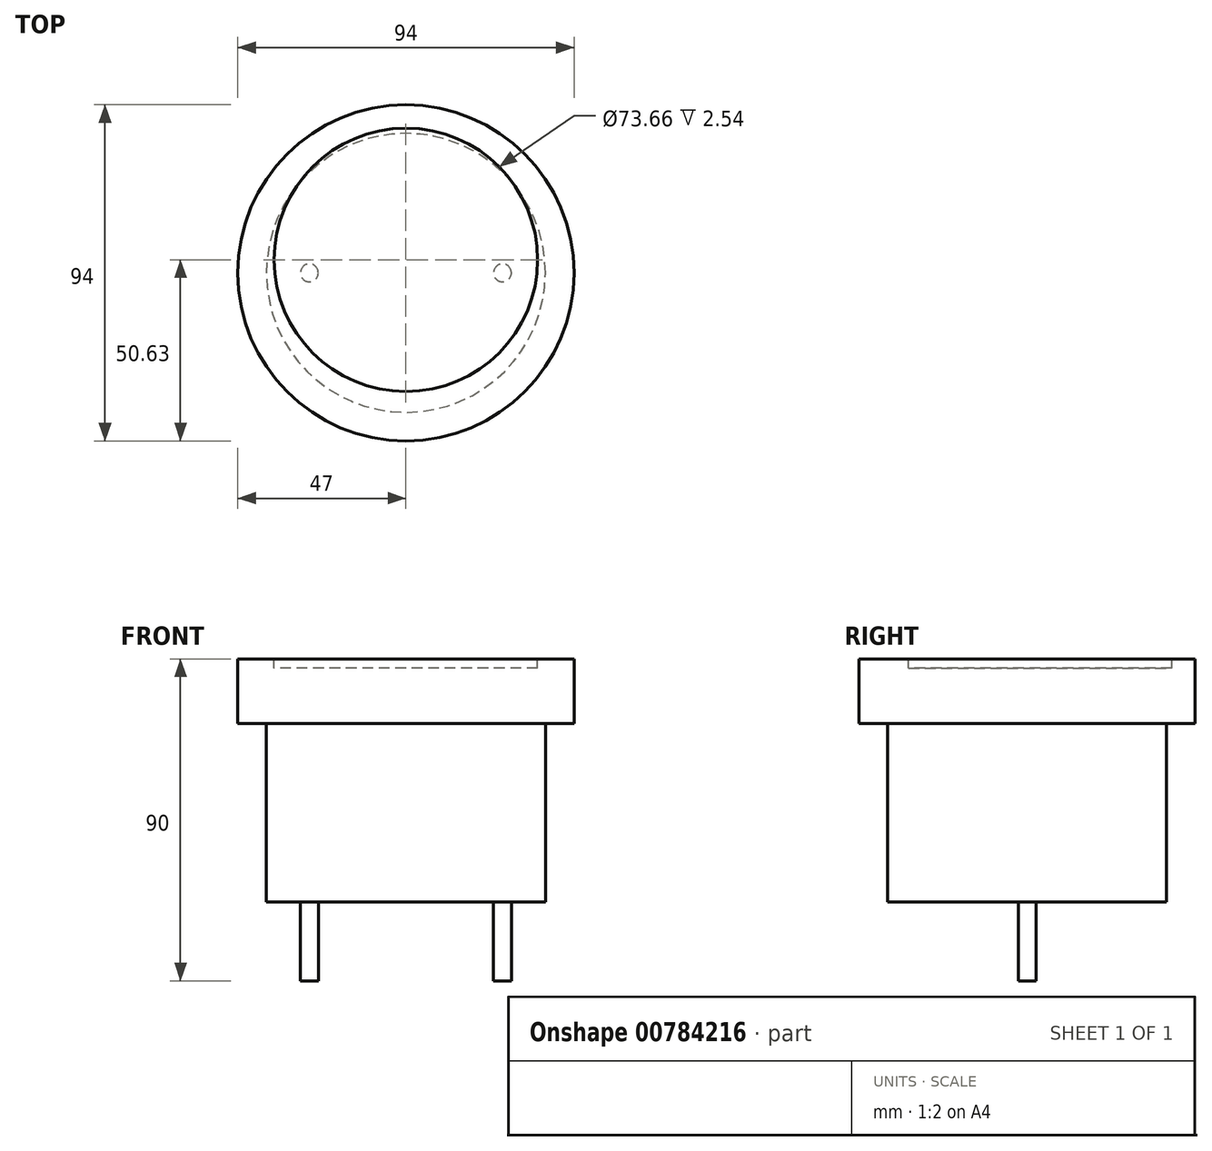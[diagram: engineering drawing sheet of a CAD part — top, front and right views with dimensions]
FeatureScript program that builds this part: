
annotation { "Feature Type Name" : "Feature", "Feature Type Description" : "" }
export const myFeature = defineFeature(function(context is Context, id is Id, definition is map)
    precondition{}
    {
        {
            var Q0;
            Q0=qCreatedBy(makeId("Top.planeOp"),FACE);
            var sketch = newSketch(context, id + "F0", { "sketchPlane" : qUnion([Q0])});
            skCircle(sketch, "E0", {"center": v(0, 0) * mm, "radius": 47 * mm});
            skSolve(sketch);
        }
        {
            var Q0;
            Q0=makeQuery(id+"F0.imprint","IMPRINT",FACE,{"disambiguationData":[TD([[makeQuery(id+"F0.imprint","IMPRINT",EDGE,{"derivedFrom":sQuery(id+"F0.wireOp",EDGE,"E0")}),1.0]])]});
            extrude(context, id + "F1", {"entities" : qUnion([Q0]), "depth" : 18 * mm, "offsetDistance" : 25.4 * mm});
        }
        {
            var Q0;
            Q0=makeQuery(id+"F1.opExtrude","CAP_FACE",FACE,{"disambiguationData":[OSD([sQuery(id+"F0.wireOp",EDGE,"E0")])],"isStart":true});
            var sketch = newSketch(context, id + "F2", { "sketchPlane" : qUnion([Q0])});
            skCircle(sketch, "E1", {"center": v(0, 0) * mm, "radius": 39 * mm});
            skSolve(sketch);
        }
        {
            var Q0;
            Q0=makeQuery(id+"F2.imprint","IMPRINT",FACE,{"disambiguationData":[TD([[makeQuery(id+"F2.imprint","IMPRINT",EDGE,{"derivedFrom":sQuery(id+"F2.wireOp",EDGE,"E1")}),1.0]])]});
            extrude(context, id + "F3", {"entities" : qUnion([Q0]), "operationType" : NewBodyOperationType.ADD, "depth" : 50 * mm, "offsetDistance" : 25.4 * mm});
        }
        {
            var Q0;
            Q0=makeQuery(id+"F3.opExtrude","CAP_FACE",FACE,{"disambiguationData":[OSD([sQuery(id+"F2.wireOp",EDGE,"E1")])],"isStart":false});
            var sketch = newSketch(context, id + "F4", { "sketchPlane" : qUnion([Q0])});
            skCircle(sketch, "E2", {"center": v(-27, 0) * mm, "radius": 2.5 * mm});
            skCircle(sketch, "E3", {"center": v(27, 0) * mm, "radius": 2.5 * mm});
            skSolve(sketch);
        }
        {
            var Q0;
            Q0=makeQuery(id+"F4.imprint","IMPRINT",FACE,{"disambiguationData":[TD([[makeQuery(id+"F4.imprint","IMPRINT",EDGE,{"derivedFrom":sQuery(id+"F4.wireOp",EDGE,"E2")}),1.0]])]});
            var Q1;
            Q1=makeQuery(id+"F4.imprint","IMPRINT",FACE,{"disambiguationData":[TD([[makeQuery(id+"F4.imprint","IMPRINT",EDGE,{"derivedFrom":sQuery(id+"F4.wireOp",EDGE,"E3")}),1.0]])]});
            extrude(context, id + "F5", {"entities" : qUnion([Q0, Q1]), "operationType" : NewBodyOperationType.ADD, "depth" : 22 * mm, "offsetDistance" : 25.4 * mm});
        }
        {
            var Q0;
            Q0=makeQuery(id+"F1.opExtrude","CAP_FACE",FACE,{"disambiguationData":[OSD([sQuery(id+"F0.wireOp",EDGE,"E0")])],"isStart":false});
            var sketch = newSketch(context, id + "F6", { "sketchPlane" : qUnion([Q0])});
            skCircle(sketch, "E4", {"center": v(0, 3.63) * mm, "radius": 36.83 * mm});
            skSolve(sketch);
        }
        {
            var Q0;
            Q0=makeQuery(id+"F6.imprint","IMPRINT",FACE,{"disambiguationData":[TD([[makeQuery(id+"F6.imprint","IMPRINT",EDGE,{"derivedFrom":sQuery(id+"F6.wireOp",EDGE,"E4")}),1.0]])]});
            extrude(context, id + "F7", {"entities" : qUnion([Q0]), "operationType" : NewBodyOperationType.REMOVE, "oppositeDirection" : true, "depth" : 2.54 * mm, "offsetDistance" : 25.4 * mm});
        }
    });
